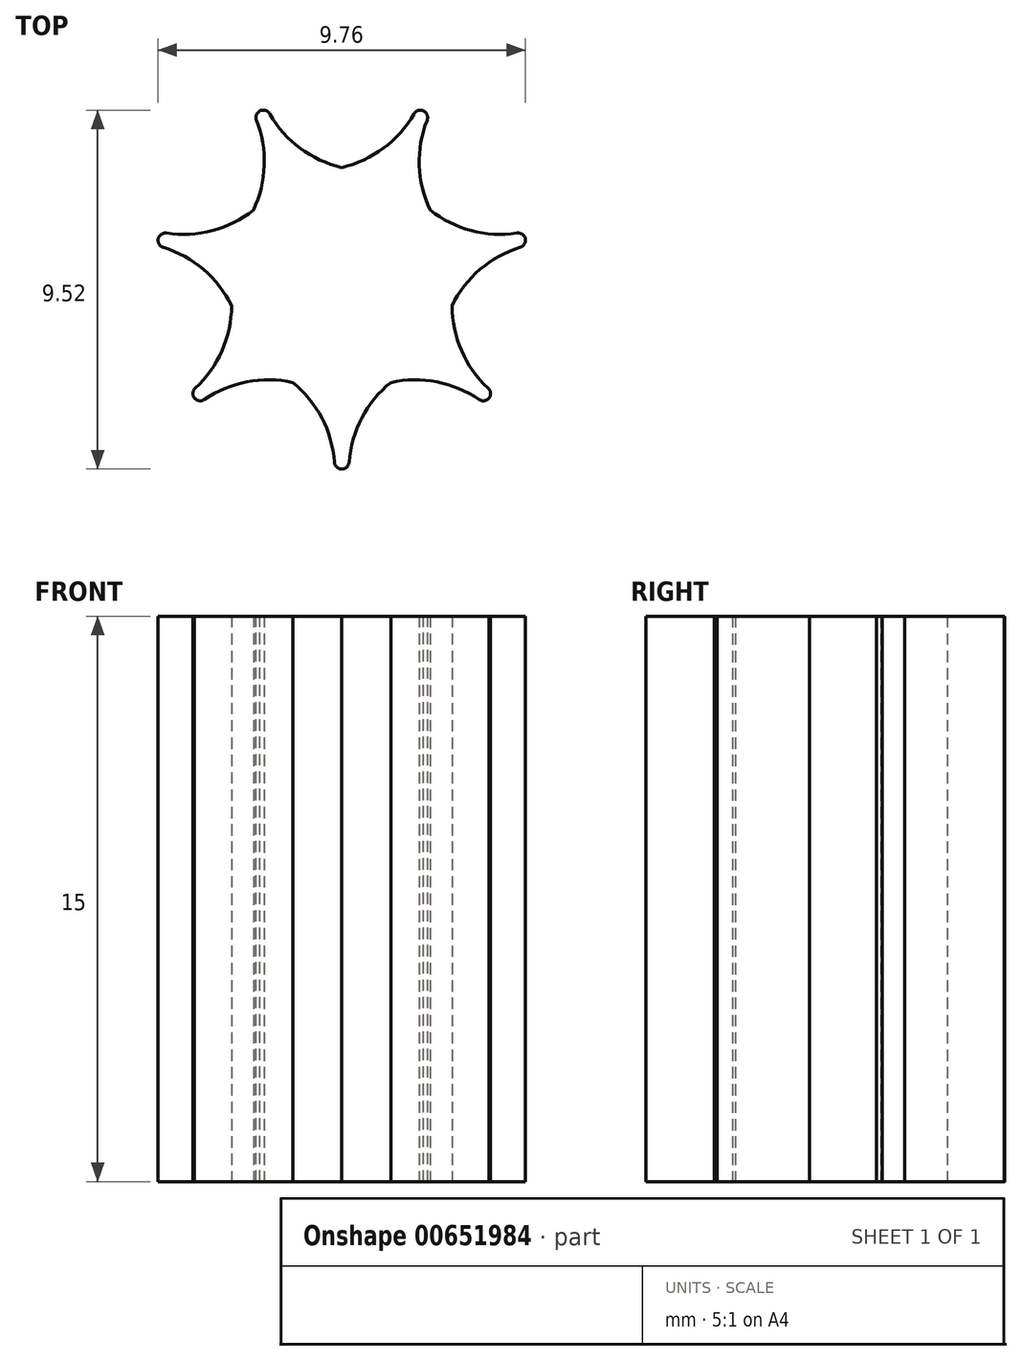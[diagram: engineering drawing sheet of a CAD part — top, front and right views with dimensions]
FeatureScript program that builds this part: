
annotation { "Feature Type Name" : "Feature", "Feature Type Description" : "" }
export const myFeature = defineFeature(function(context is Context, id is Id, definition is map)
    precondition{}
    {
        {
            var Q0;
            Q0=qCreatedBy(makeId("Top.planeOp"),FACE);
            var sketch = newSketch(context, id + "F0", { "sketchPlane" : qUnion([Q0])});
            skCircle(sketch, "E0", {"center": v(0, 0) * mm, "radius": 10 * mm});
            skCircle(sketch, "E1", {"center": v(0, 0) * mm, "radius": 5 * mm});
            skArc(sketch, "E2", {"start": v(-2, 4.58) * mm, "mid": v(-1.18, 3.57) * mm, "end": v(0, 3) * mm});
            skArc(sketch, "E3", {"start": v(0, 3) * mm, "mid": v(1.18, 3.57) * mm, "end": v(2, 4.58) * mm});
            skArc(sketch, "E4.1.0", {"start": v(-4.83, 1.3) * mm, "mid": v(-3.52, 1.3) * mm, "end": v(-2.35, 1.87) * mm});
            skArc(sketch, "E4.1.1", {"start": v(-2.35, 1.87) * mm, "mid": v(-2.06, 3.14) * mm, "end": v(-2.34, 4.42) * mm});
            skArc(sketch, "E4.2.0", {"start": v(-4.02, -2.97) * mm, "mid": v(-3.22, -1.94) * mm, "end": v(-2.92, -0.67) * mm});
            skArc(sketch, "E4.2.1", {"start": v(-2.92, -0.67) * mm, "mid": v(-3.74, 0.35) * mm, "end": v(-4.91, 0.93) * mm});
            skArc(sketch, "E4.3.0", {"start": v(-0.19, -5) * mm, "mid": v(-0.49, -3.73) * mm, "end": v(-1.3, -2.7) * mm});
            skArc(sketch, "E4.3.1", {"start": v(-1.3, -2.7) * mm, "mid": v(-2.6, -2.7) * mm, "end": v(-3.8, -3.26) * mm});
            skArc(sketch, "E4.4.0", {"start": v(3.8, -3.26) * mm, "mid": v(2.6, -2.7) * mm, "end": v(1.3, -2.7) * mm});
            skArc(sketch, "E4.4.1", {"start": v(1.3, -2.7) * mm, "mid": v(0.49, -3.73) * mm, "end": v(0.19, -5) * mm});
            skArc(sketch, "E4.5.0", {"start": v(4.91, 0.93) * mm, "mid": v(3.74, 0.35) * mm, "end": v(2.92, -0.67) * mm});
            skArc(sketch, "E4.5.1", {"start": v(2.92, -0.67) * mm, "mid": v(3.22, -1.94) * mm, "end": v(4.02, -2.97) * mm});
            skArc(sketch, "E4.6.0", {"start": v(2.34, 4.42) * mm, "mid": v(2.06, 3.14) * mm, "end": v(2.35, 1.87) * mm});
            skArc(sketch, "E4.6.1", {"start": v(2.35, 1.87) * mm, "mid": v(3.52, 1.3) * mm, "end": v(4.83, 1.3) * mm});
            skSolve(sketch);
        }
        {
            var Q0;
            {var subQ1=sQuery(id+"F0.wireOp",EDGE,"E2");Q0=makeQuery(id+"F0.imprint","IMPRINT",FACE,{"disambiguationData":[TD([[makeQuery(id+"F0.imprint","IMPRINT",EDGE,{"derivedFrom":subQ1}),-1.0]])]});}
            extrude(context, id + "F1", {"entities" : qUnion([Q0]), "depth" : 15 * mm, "offsetDistance" : 25 * mm});
        }
        {
            var Q0;
            Q0=makeQuery(id+"F1.opExtrude","SWEPT_EDGE",EDGE,{"disambiguationData":[OSD([sQuery(id+"F0.wireOp",EDGE,"E1"),sQuery(id+"F0.wireOp",EDGE,"E4.3.1")])]});
            var Q1;
            Q1=makeQuery(id+"F1.opExtrude","SWEPT_EDGE",EDGE,{"disambiguationData":[OSD([sQuery(id+"F0.wireOp",EDGE,"E1"),sQuery(id+"F0.wireOp",EDGE,"E4.2.0")])]});
            var Q2;
            Q2=makeQuery(id+"F1.opExtrude","SWEPT_EDGE",EDGE,{"disambiguationData":[OSD([sQuery(id+"F0.wireOp",EDGE,"E1"),sQuery(id+"F0.wireOp",EDGE,"E4.3.0")])]});
            var Q3;
            Q3=makeQuery(id+"F1.opExtrude","SWEPT_EDGE",EDGE,{"disambiguationData":[OSD([sQuery(id+"F0.wireOp",EDGE,"E1"),sQuery(id+"F0.wireOp",EDGE,"E4.4.1")])]});
            var Q4;
            Q4=makeQuery(id+"F1.opExtrude","SWEPT_EDGE",EDGE,{"disambiguationData":[OSD([sQuery(id+"F0.wireOp",EDGE,"E1"),sQuery(id+"F0.wireOp",EDGE,"E4.4.0")])]});
            var Q5;
            Q5=makeQuery(id+"F1.opExtrude","SWEPT_EDGE",EDGE,{"disambiguationData":[OSD([sQuery(id+"F0.wireOp",EDGE,"E1"),sQuery(id+"F0.wireOp",EDGE,"E4.5.1")])]});
            var Q6;
            Q6=makeQuery(id+"F1.opExtrude","SWEPT_EDGE",EDGE,{"disambiguationData":[OSD([sQuery(id+"F0.wireOp",EDGE,"E1"),sQuery(id+"F0.wireOp",EDGE,"E4.5.0")])]});
            var Q7;
            Q7=makeQuery(id+"F1.opExtrude","SWEPT_EDGE",EDGE,{"disambiguationData":[OSD([sQuery(id+"F0.wireOp",EDGE,"E1"),sQuery(id+"F0.wireOp",EDGE,"E4.6.1")])]});
            var Q8;
            Q8=makeQuery(id+"F1.opExtrude","SWEPT_EDGE",EDGE,{"disambiguationData":[OSD([sQuery(id+"F0.wireOp",EDGE,"E1"),sQuery(id+"F0.wireOp",EDGE,"E4.6.0")])]});
            var Q9;
            Q9=makeQuery(id+"F1.opExtrude","SWEPT_EDGE",EDGE,{"disambiguationData":[OSD([sQuery(id+"F0.wireOp",EDGE,"E1"),sQuery(id+"F0.wireOp",EDGE,"E3")])]});
            var Q10;
            Q10=makeQuery(id+"F1.opExtrude","SWEPT_EDGE",EDGE,{"disambiguationData":[OSD([sQuery(id+"F0.wireOp",EDGE,"E1"),sQuery(id+"F0.wireOp",EDGE,"E2")])]});
            var Q11;
            Q11=makeQuery(id+"F1.opExtrude","SWEPT_EDGE",EDGE,{"disambiguationData":[OSD([sQuery(id+"F0.wireOp",EDGE,"E1"),sQuery(id+"F0.wireOp",EDGE,"E4.1.1")])]});
            var Q12;
            Q12=makeQuery(id+"F1.opExtrude","SWEPT_EDGE",EDGE,{"disambiguationData":[OSD([sQuery(id+"F0.wireOp",EDGE,"E1"),sQuery(id+"F0.wireOp",EDGE,"E4.2.1")])]});
            var Q13;
            Q13=makeQuery(id+"F1.opExtrude","SWEPT_EDGE",EDGE,{"disambiguationData":[OSD([sQuery(id+"F0.wireOp",EDGE,"E1"),sQuery(id+"F0.wireOp",EDGE,"E4.1.0")])]});
            fillet(context, id + "F2", {"entities" : qUnion([Q0, Q1, Q2, Q3, Q4, Q5, Q6, Q7, Q8, Q9, Q10, Q11, Q12, Q13]), "radius" : .2 * mm, "tangentPropagation" : true, "allowEdgeOverflow" : false});
        }
    });
